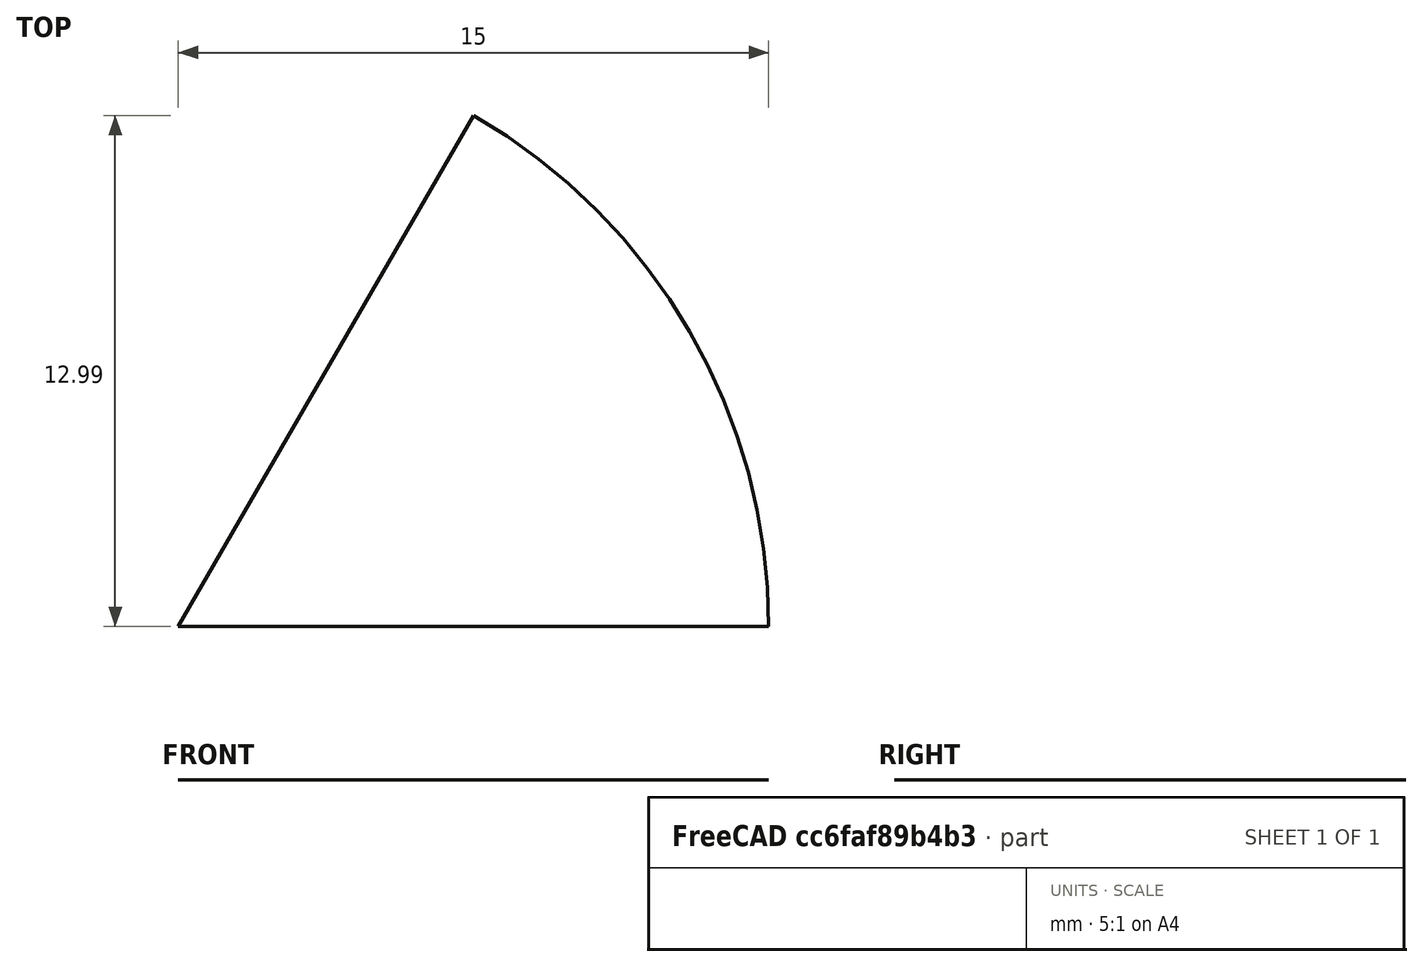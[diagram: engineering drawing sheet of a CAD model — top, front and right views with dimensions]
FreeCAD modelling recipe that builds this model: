
FCSTD DOCUMENT  (FreeCAD 0.18R4 (GitTag))
Label: pie1
License: All rights reserved
LicenseURL: http://en.wikipedia.org/wiki/All_rights_reserved
objects: Sketcher::SketchObject×2, PartDesign::Body×2, Spreadsheet::Sheet×1, Surface::Filling×1
note: 5 computed .brp shape members not serialized (recipe doc carries the construction recipe); baked Part::Feature solids carry a one-line shape summary decoded from their .brp

FEATURE [Spreadsheet::Sheet] Spreadsheet  label="Variables"
  cells = A2=segmentNumber; B2(segmentNumber)=6; A3=outerDiameter; B3(outerDiameter)=30; D3=Calc Value; A4=length; B4(length)=20; D4=Input Value; A5=segmentAngle; B5(segmentAngle)==360 / segmentNumber
FEATURE [Sketcher::SketchObject] Sketch003  label="PieSketch"
  MapMode = 5
  Support = -> [XY_Plane]
  expr: Constraints[7] = Variables.outerDiameter / 2
  expr: Constraints[2] = Variables.segmentAngle
  sketch-geometry (3):
    g0: LineSegment StartX=0 StartY=0 StartZ=0 EndX=15 EndY=-4e-14 EndZ=0
    g1: LineSegment StartX=0 StartY=0 StartZ=0 EndX=7.5 EndY=12.9904 EndZ=0
    g2: ArcOfCircle CenterX=0 CenterY=0 CenterZ=0 NormalX=0 NormalY=0 NormalZ=1 AngleXU=0 Radius=15 StartAngle=-2.7e-15 EndAngle=1.0472
  constraints (8):
    c: Coincident(g0,g-1)
    c: Coincident(g1,g0)
    c: Angle(g0,g1) = 1.0472
    c: Coincident(g2,g-1)
    c: Coincident(g2,g1)
    c: Coincident(g2,g0)
    c: Angle(g-1,g0) = 0
    c: Radius(g2) = 15
FEATURE [PartDesign::Body] Body  label="TopView"
  Group = -> [Sketch003]
  Origin = -> Origin
FEATURE [Sketcher::SketchObject] Sketch  label="PieSide"
  MapMode = 5
  Support = -> [XY_Plane001]
  expr: Constraints[9] = Variables.outerDiameter
  expr: Constraints[8] = Variables.length
  sketch-geometry (4):
    g0: LineSegment StartX=-10 StartY=-15 StartZ=0 EndX=10 EndY=-15 EndZ=0
    g1: LineSegment StartX=10 StartY=-15 StartZ=0 EndX=10 EndY=15 EndZ=0
    g2: LineSegment StartX=10 StartY=15 StartZ=0 EndX=-10 EndY=15 EndZ=0
    g3: LineSegment StartX=-10 StartY=15 StartZ=0 EndX=-10 EndY=-15 EndZ=0
  constraints (10):
    c: Coincident(g0,g1)
    c: Coincident(g1,g2)
    c: Coincident(g2,g3)
    c: Coincident(g3,g0)
    c: Horizontal(g2)
    c: Vertical(g1)
    c: Symmetric(g0,g2,g-1)
    c: Symmetric(g0,g0,g-2)
    c: DistanceX(g0,g0) = 20
    c: DistanceY(g1,g1) = 30
FEATURE [PartDesign::Body] Body001  label="SideView"
  Group = -> [Sketch]
  Origin = -> Origin001
FEATURE [Surface::Filling] Surface  label="PieSketch_Surface"
  Anisotropy = false
  BoundaryEdges = -> [Sketch003]
  BoundaryOrder = [0,0,0]
  Degree = 3
  Iterations = 2
  MaximumDegree = 8
  MaximumSegments = 9
  PointsOnCurve = 15
  TolAngular = 0.01
  TolCurvature = 0.1
  Tolerance2d = 1e-05
  Tolerance3d = 0.0001
